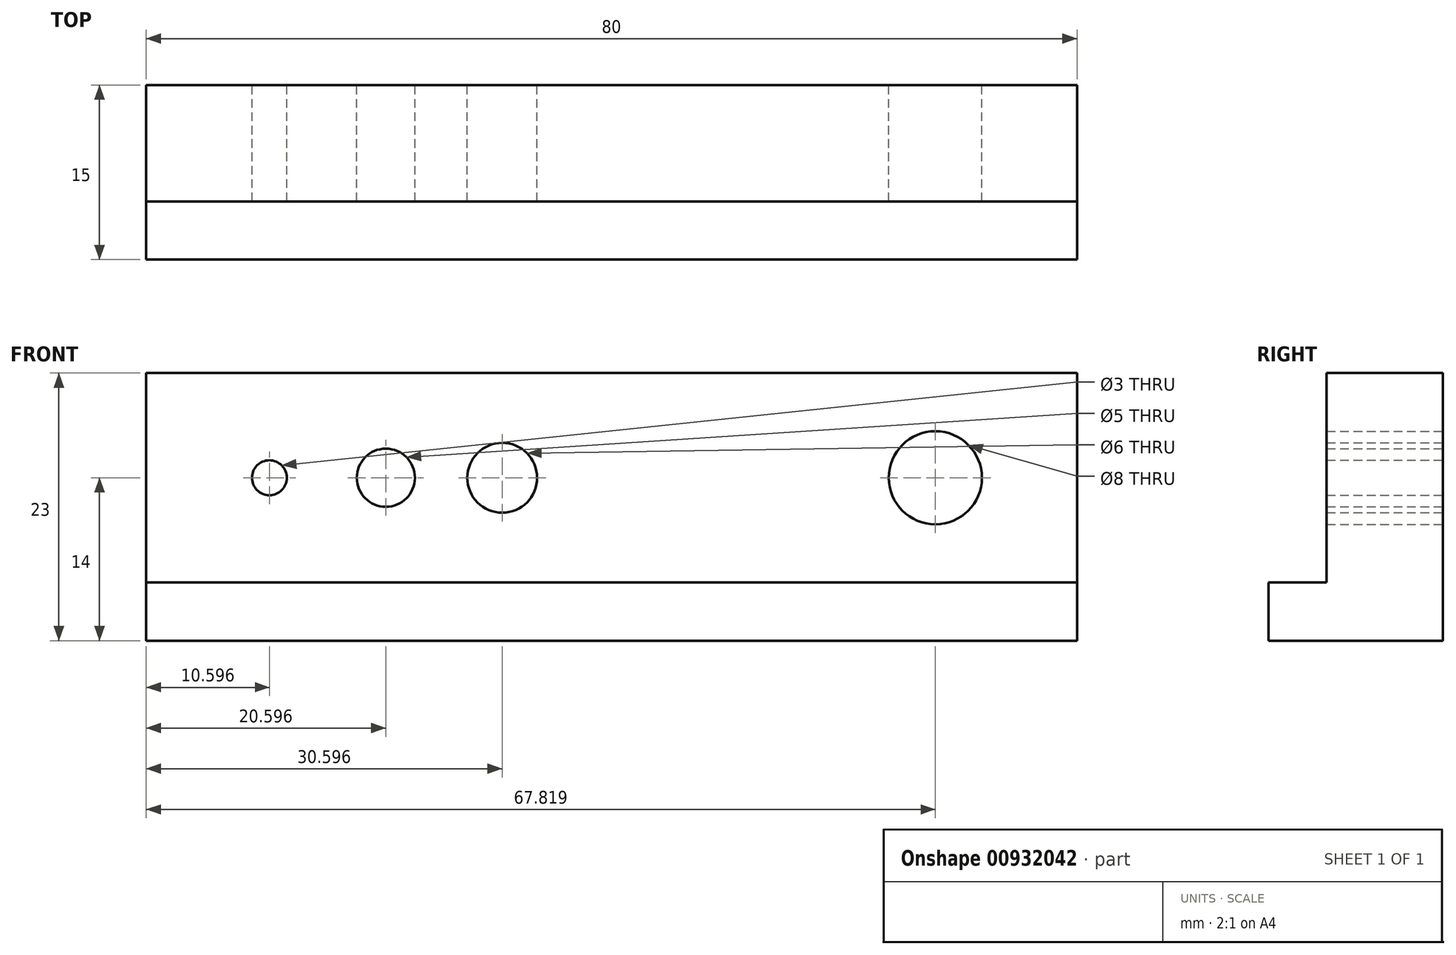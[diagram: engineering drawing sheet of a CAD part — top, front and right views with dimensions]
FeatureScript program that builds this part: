
annotation { "Feature Type Name" : "Feature", "Feature Type Description" : "" }
export const myFeature = defineFeature(function(context is Context, id is Id, definition is map)
    precondition{}
    {
        {
            var Q0;
            Q0=qCreatedBy(makeId("Front.planeOp"),FACE);
            var sketch = newSketch(context, id + "F0", { "sketchPlane" : qUnion([Q0])});
            skLineSegment(sketch, "E0.bottom", {"start": v(40, -11.5) * mm, "end": v(-40, -11.5) * mm});
            skLineSegment(sketch, "E0.top", {"start": v(40, 11.5) * mm, "end": v(-40, 11.5) * mm});
            skLineSegment(sketch, "E0.left", {"start": v(40, -11.5) * mm, "end": v(40, 11.5) * mm});
            skLineSegment(sketch, "E0.right", {"start": v(-40, -11.5) * mm, "end": v(-40, 11.5) * mm});
            skPoint(sketch, "E0.middle", {"position": v(0, 0) * mm});
            skLineSegment(sketch, "E1", {"start": v(-40, -6.5) * mm, "end": v(40, -6.5) * mm});
            skCircle(sketch, "E2", {"center": v(-29.4, 2.5) * mm, "radius": 1.5 * mm});
            skCircle(sketch, "E3", {"center": v(-19.4, 2.5) * mm, "radius": 2.5 * mm});
            skCircle(sketch, "E4", {"center": v(-9.4, 2.5) * mm, "radius": 3 * mm});
            skCircle(sketch, "E5", {"center": v(27.82, 2.5) * mm, "radius": 4 * mm});
            skSolve(sketch);
        }
        {
            var Q0;
            {var subQ1=sQuery(id+"F0.wireOp",EDGE,"E0.top");Q0=makeQuery(id+"F0.imprint","IMPRINT",FACE,{"disambiguationData":[TD([[makeQuery(id+"F0.imprint","IMPRINT",EDGE,{"derivedFrom":subQ1}),1.0]])]});}
            var Q1;
            {var subQ0=sQuery(id+"F0.wireOp",EDGE,"E0.bottom");Q1=makeQuery(id+"F0.imprint","IMPRINT",FACE,{"disambiguationData":[TD([[makeQuery(id+"F0.imprint","IMPRINT",EDGE,{"derivedFrom":subQ0}),-1.0]])]});}
            extrude(context, id + "F1", {"entities" : qUnion([Q0, Q1]), "depth" : 10 * mm, "offsetDistance" : 25.4 * mm});
        }
        {
            var Q0;
            Q0=makeQuery(id+"F1.opExtrude","CAP_FACE",FACE,{"disambiguationData":[OSD([sQuery(id+"F0.wireOp",EDGE,"E0.bottom"),sQuery(id+"F0.wireOp",EDGE,"E0.top"),sQuery(id+"F0.wireOp",EDGE,"E0.left"),sQuery(id+"F0.wireOp",EDGE,"E0.right"),sQuery(id+"F0.wireOp",EDGE,"E2"),sQuery(id+"F0.wireOp",EDGE,"E3"),sQuery(id+"F0.wireOp",EDGE,"E4"),sQuery(id+"F0.wireOp",EDGE,"E5")])],"isStart":false});
            var sketch = newSketch(context, id + "F2", { "sketchPlane" : qUnion([Q0])});
            skLineSegment(sketch, "E6.bottom", {"start": v(-40, -11.5) * mm, "end": v(40, -11.5) * mm});
            skLineSegment(sketch, "E6.top", {"start": v(-40, -6.5) * mm, "end": v(40, -6.5) * mm});
            skLineSegment(sketch, "E6.left", {"start": v(-40, -11.5) * mm, "end": v(-40, -6.5) * mm});
            skLineSegment(sketch, "E6.right", {"start": v(40, -11.5) * mm, "end": v(40, -6.5) * mm});
            skSolve(sketch);
        }
        {
            var Q0;
            Q0=makeQuery(id+"F2.imprint","IMPRINT",FACE,{"disambiguationData":[TD([[makeQuery(id+"F2.imprint","IMPRINT",EDGE,{"derivedFrom":sQuery(id+"F2.wireOp",EDGE,"E6.bottom")}),-1.0]])]});
            extrude(context, id + "F3", {"entities" : qUnion([Q0]), "operationType" : NewBodyOperationType.ADD, "depth" : 5 * mm, "offsetDistance" : 25.4 * mm});
        }
    });
